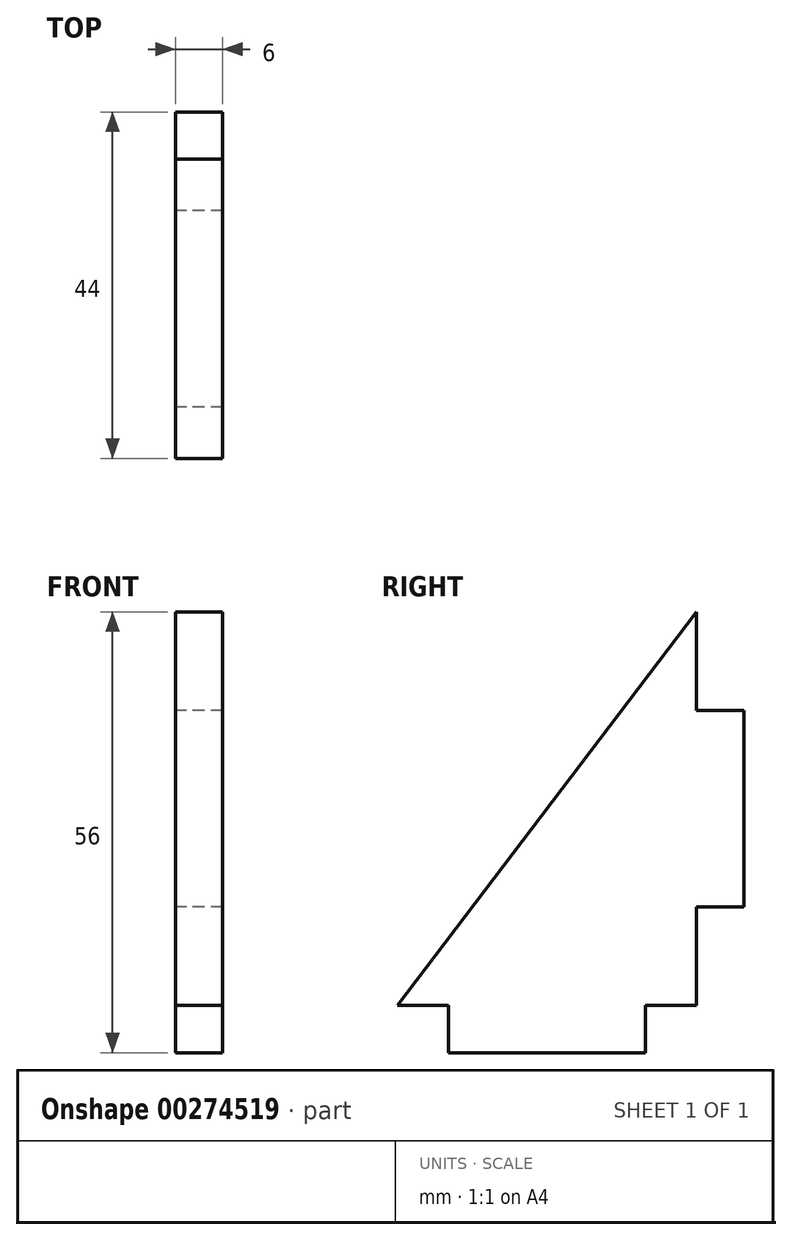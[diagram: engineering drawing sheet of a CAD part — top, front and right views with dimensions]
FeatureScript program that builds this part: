
annotation { "Feature Type Name" : "Feature", "Feature Type Description" : "" }
export const myFeature = defineFeature(function(context is Context, id is Id, definition is map)
    precondition{}
    {
        {
            var Q0;
            Q0=qCreatedBy(makeId("Right.planeOp"),FACE);
            var sketch = newSketch(context, id + "F0", { "sketchPlane" : qUnion([Q0])});
            skLineSegment(sketch, "E0", {"start": v(14.7, 32.1) * mm, "end": v(14.7, 19.6) * mm});
            skLineSegment(sketch, "E1", {"start": v(14.7, -17.9) * mm, "end": v(8.2, -17.9) * mm});
            skLineSegment(sketch, "E2", {"start": v(-23.3, -17.9) * mm, "end": v(14.7, 32.1) * mm});
            skLineSegment(sketch, "E3.bottom", {"start": v(14.7, 19.6) * mm, "end": v(20.7, 19.6) * mm});
            skLineSegment(sketch, "E3.top", {"start": v(14.7, -5.4) * mm, "end": v(20.7, -5.4) * mm});
            skLineSegment(sketch, "E3.right", {"start": v(20.7, 19.6) * mm, "end": v(20.7, -5.4) * mm});
            skLineSegment(sketch, "E4.top", {"start": v(-16.8, -23.9) * mm, "end": v(8.2, -23.9) * mm});
            skLineSegment(sketch, "E4.left", {"start": v(-16.8, -17.9) * mm, "end": v(-16.8, -23.9) * mm});
            skLineSegment(sketch, "E4.right", {"start": v(8.2, -17.9) * mm, "end": v(8.2, -23.9) * mm});
            skLineSegment(sketch, "E5.trimOffspring", {"start": v(14.7, -5.4) * mm, "end": v(14.7, -17.9) * mm});
            skLineSegment(sketch, "E6.trimOffspring", {"start": v(-16.8, -17.9) * mm, "end": v(-23.3, -17.9) * mm});
            skSolve(sketch);
        }
        {
            var Q0;
            Q0 = qSketchRegion(id + "F0", true);
            extrude(context, id + "F1", {"entities" : qUnion([Q0]), "depth" : 6 * mm});
        }
    });
